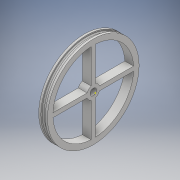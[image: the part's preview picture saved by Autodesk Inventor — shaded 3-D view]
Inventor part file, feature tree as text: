
AUTODESK INVENTOR PART (.ipt)
format: ipt  version: 2018 (Build 220112000, 112)  size: 198,656 bytes
history: native  units: mm
features: sketch x11, extrude x10, fillet x1, pattern_circular x1
ambient origin geometry x8: Origin, YZ Plane, XZ Plane, XY Plane, X Axis, Y Axis, Z Axis, Center Point
bodies: Solid1 (feature_tree)
feature tree (23):
  extrude  "Extrusion1"  Depth=5.0mm TaperAngle=0.0deg
  extrude  "Extrusion2"  Depth=2.0mm TaperAngle=0.0deg
  extrude  "Extrusion3"  Depth=0.5mm
  fillet  "Fillet1"  Radius=37.0mm
  extrude  "Extrusion4"  Depth=4.0mm
  extrude  "Extrusion5"  Depth=6.0mm TaperAngle=0.0deg
  sketch  "Sketch6"  dims[d16=1.0mm d17=0.0mm d18=1.0mm d19=0.0mm]
  sketch  "Sketch7"  dims[d20=1.0mm d21=0.0mm d22=1.0mm]
  extrude  "Extrusion6"  Depth=1.0mm TaperAngle=0.0deg
  extrude  "Extrusion7"  Depth=1.0mm
  extrude  "Extrusion8"  Depth=2.0mm
  extrude  "Extrusion9"  Depth=4.0mm TaperAngle=360.0deg
  pattern_circular  "Circular Pattern1"  [2 undecoded]
  extrude  "Extrusion10"  [1 undecoded]
  sketch  "Sketch1"  dims[d0=40.0mm d1=5.0mm d2=0.0mm]
  sketch  "Sketch2"  dims[d3=42.0mm d4=2.0mm d5=0.0mm]
  sketch  "Sketch3"  dims[d6=2.0mm d7=0.0mm d8=0.5mm d9=37.0mm]
  sketch  "Sketch4"  dims[d10=6.0mm d11=0.0mm d12=4.0mm]
  sketch  "Sketch5"  dims[d13=6.0mm d14=6.0mm d15=0.0mm]
  sketch  "Sketch8"  dims[d23=2.0mm d24=2.0mm]
  sketch  "Sketch9"  dims[d25=4.0mm d26=0.0mm d27=40.0mm d28=360.0deg]
  sketch  "Sketch10"  dims[d30=3.0mm]
  sketch  "Sketch11"  dims[d31=4.0mm d32=0.0mm]
note: 3 required parameter values undecoded (feature->parameter linkage not recoverable at this tier; creation-order binding heuristic only, values carry confidence <= 0.55)
